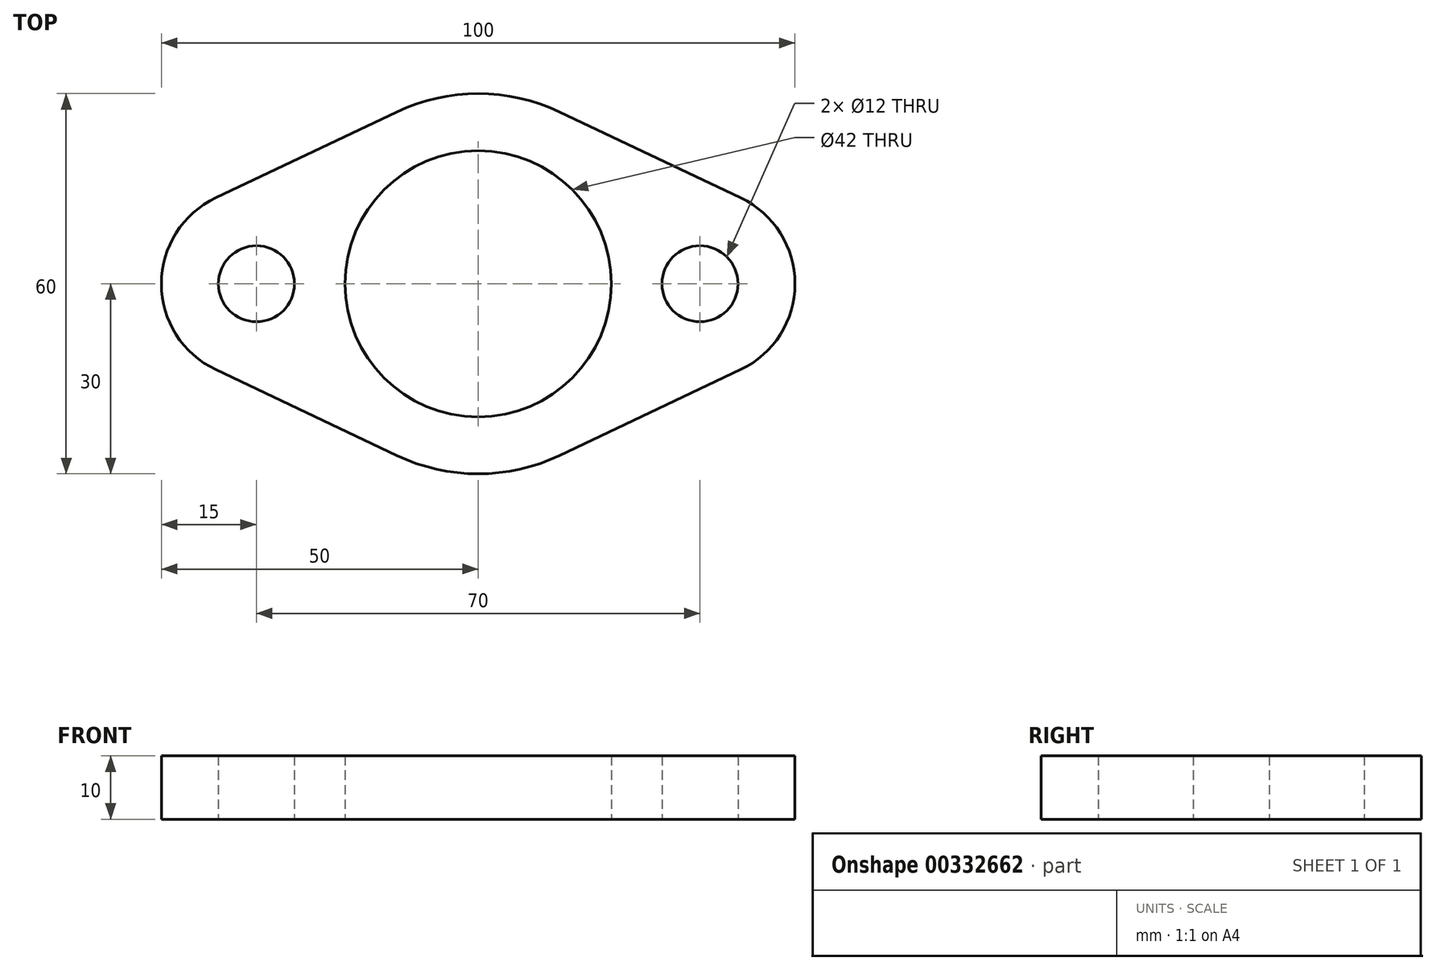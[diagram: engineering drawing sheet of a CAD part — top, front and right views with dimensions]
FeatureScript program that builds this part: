
annotation { "Feature Type Name" : "Feature", "Feature Type Description" : "" }
export const myFeature = defineFeature(function(context is Context, id is Id, definition is map)
    precondition{}
    {
        {
            var Q0;
            Q0=qCreatedBy(makeId("Top.planeOp"),FACE);
            var sketch = newSketch(context, id + "F0", { "sketchPlane" : qUnion([Q0])});
            skArc(sketch, "E0", {"start": v(-12.86, -27.1) * mm, "mid": v(0, -30) * mm, "end": v(12.86, -27.1) * mm});
            skCircle(sketch, "E1", {"center": v(0, 0) * mm, "radius": 21 * mm});
            skArc(sketch, "E2", {"start": v(41.43, -13.55) * mm, "mid": v(50, 0) * mm, "end": v(41.43, 13.55) * mm});
            skArc(sketch, "E3", {"start": v(-41.43, 13.55) * mm, "mid": v(-50, 0) * mm, "end": v(-41.43, -13.55) * mm});
            skCircle(sketch, "E4", {"center": v(-35, 0) * mm, "radius": 6 * mm});
            skCircle(sketch, "E5", {"center": v(35, 0) * mm, "radius": 6 * mm});
            skLineSegment(sketch, "E6", {"start": v(-41.43, 13.55) * mm, "end": v(-12.86, 27.1) * mm});
            skLineSegment(sketch, "E7", {"start": v(12.86, 27.1) * mm, "end": v(41.43, 13.55) * mm});
            skLineSegment(sketch, "E8", {"start": v(-41.43, -13.55) * mm, "end": v(-12.86, -27.1) * mm});
            skLineSegment(sketch, "E9", {"start": v(12.86, -27.1) * mm, "end": v(41.43, -13.55) * mm});
            skArc(sketch, "E10.trimOffspring", {"start": v(12.86, 27.1) * mm, "mid": v(0, 30) * mm, "end": v(-12.86, 27.1) * mm});
            skSolve(sketch);
        }
        {
            var Q0;
            Q0=makeQuery(id+"F0.imprint","IMPRINT",FACE,{"disambiguationData":[TD([[makeQuery(id+"F0.imprint","IMPRINT",EDGE,{"derivedFrom":sQuery(id+"F0.wireOp",EDGE,"E0")}),1.0]])]});
            extrude(context, id + "F1", {"entities" : qUnion([Q0]), "depth" : 10 * mm});
        }
    });
